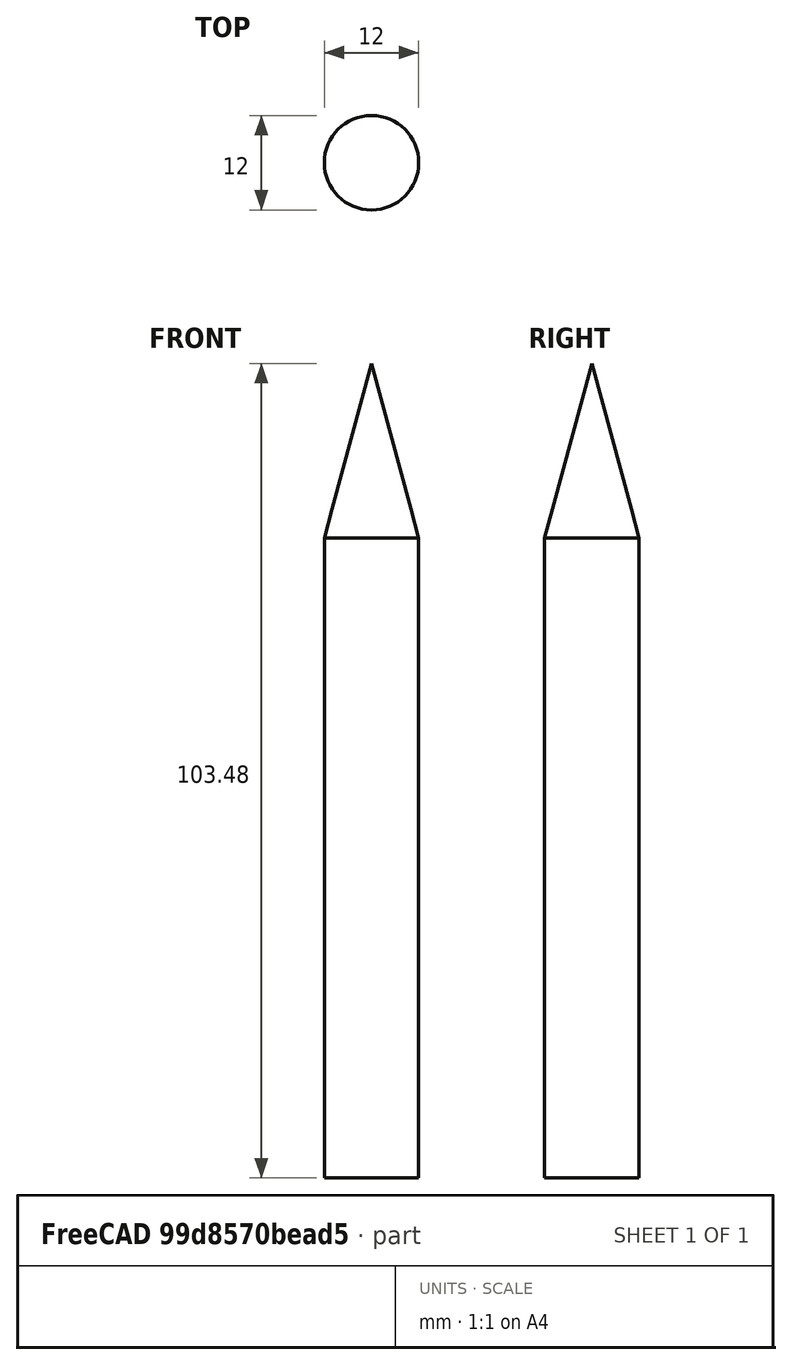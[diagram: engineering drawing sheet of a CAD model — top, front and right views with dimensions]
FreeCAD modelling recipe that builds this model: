
FCSTD DOCUMENT  (FreeCAD 0.19R24291 (Git))
Label: thrust vector marker
License: All rights reserved
LicenseURL: http://en.wikipedia.org/wiki/All_rights_reserved
objects: Sketcher::SketchObject×1, PartDesign::Revolution×1, PartDesign::Body×1
note: 4 computed .brp shape members not serialized (recipe doc carries the construction recipe); baked Part::Feature solids carry a one-line shape summary decoded from their .brp

FEATURE [Sketcher::SketchObject] Sketch
  FullyConstrained = false
  MapMode = 5
  Placement = pos=(0,0,0) rot=(1,0,0;1.5708rad)
  Support = -> [XZ_Plane]
  sketch-geometry (9):
    g0: LineSegment StartX=0 StartY=0 StartZ=0 EndX=-6 EndY=0 EndZ=0
    g1: LineSegment StartX=-6 StartY=0 StartZ=0 EndX=-6 EndY=60 EndZ=0
    g2: LineSegment StartX=0 StartY=85 StartZ=0 EndX=0 EndY=0 EndZ=0
    g3: LineSegment StartX=0 StartY=85 StartZ=0 EndX=-5 EndY=85 EndZ=0
    g4: LineSegment StartX=-5 StartY=85 StartZ=0 EndX=-6 EndY=81.3044 EndZ=0
    g5: LineSegment StartX=-5 StartY=85 StartZ=0 EndX=0 EndY=103.478 EndZ=0
    g6: LineSegment StartX=-6 StartY=60 StartZ=0 EndX=-6 EndY=81.3044 EndZ=0
    g7: GeomPoint X=-12.3299 Y=78.4324 Z=0
    g8: LineSegment StartX=0 StartY=85 StartZ=0 EndX=0 EndY=103.478 EndZ=0
  constraints (21):
    c: Coincident(g0,g1)
    c: Vertical(g2)
    c: Coincident(g0,g2)
    c: Horizontal(g0)
    c: Vertical(g1)
    c: Coincident(g0,g-1)
    c: Coincident(g3,g2)
    c: Horizontal(g3)
    c: Coincident(g4,g3)
    c: Distance(g0) = 6
    c: Distance(g2) = 85
    c: Distance(g1) = 60
    c: Distance(g3) = 5
    c: Coincident(g5,g3)
    c: Coincident(g6,g1)
    c: Vertical(g6)
    c: Parallel(g5,g4)
    c: Coincident(g8,g2)
    c: Coincident(g5,g8)
    c: Vertical(g8)
    c: Coincident(g4,g6)
FEATURE [PartDesign::Revolution] Revolution
  Angle = 360
  Axis = (0,-2e-16,1)
  Base = (0,0,0)
  Placement = pos=(0,0,0) rot=(1,0,0;1.5708rad)
  Profile = -> Sketch
  ReferenceAxis = -> Sketch [V_Axis]
FEATURE [PartDesign::Body] Body
  Group = -> [Sketch,Revolution]
  Origin = -> Origin
  Tip = -> Revolution
